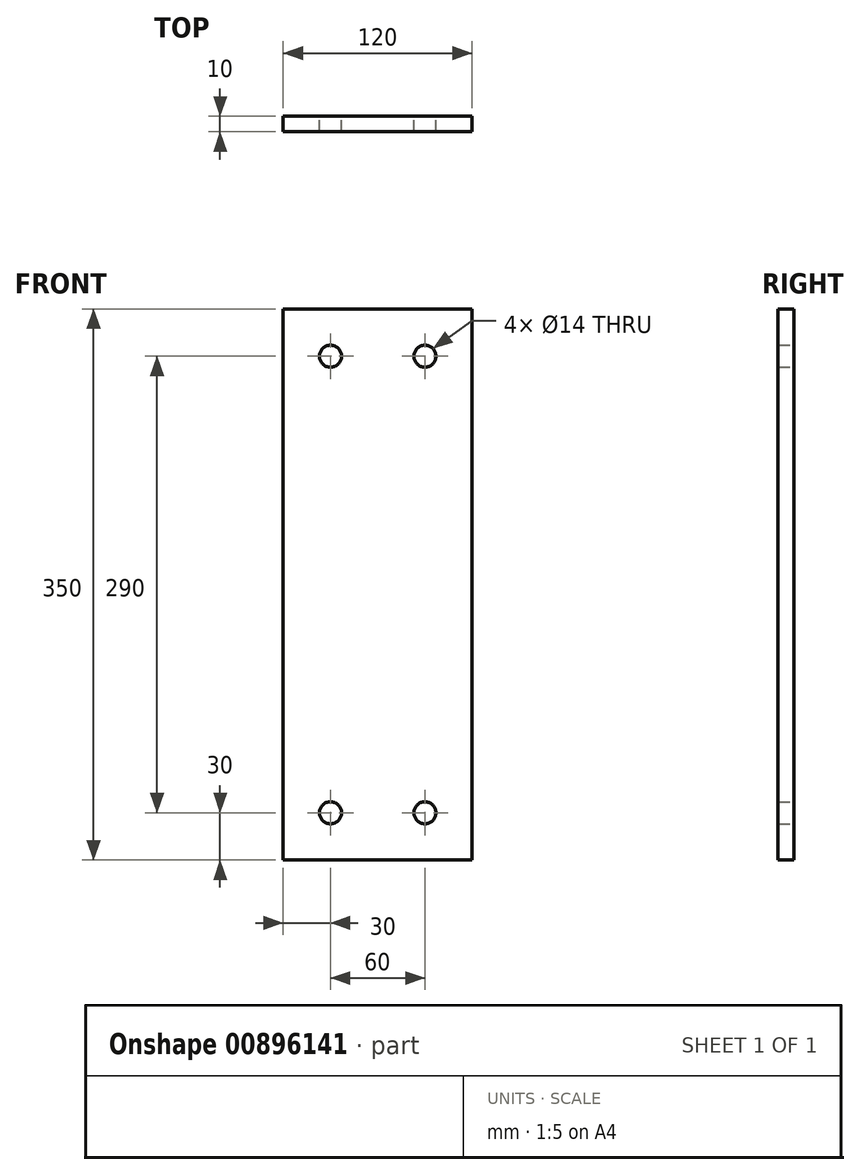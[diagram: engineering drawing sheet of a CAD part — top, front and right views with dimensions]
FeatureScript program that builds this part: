
annotation { "Feature Type Name" : "Feature", "Feature Type Description" : "" }
export const myFeature = defineFeature(function(context is Context, id is Id, definition is map)
    precondition{}
    {
        {
            var Q0;
            Q0=qCreatedBy(makeId("Front.planeOp"),FACE);
            var sketch = newSketch(context, id + "F0", { "sketchPlane" : qUnion([Q0])});
            skLineSegment(sketch, "E0.bottom", {"start": v(60, 175) * mm, "end": v(-60, 175) * mm});
            skLineSegment(sketch, "E0.top", {"start": v(60, -175) * mm, "end": v(-60, -175) * mm});
            skLineSegment(sketch, "E0.left", {"start": v(60, 175) * mm, "end": v(60, -175) * mm});
            skLineSegment(sketch, "E0.right", {"start": v(-60, 175) * mm, "end": v(-60, -175) * mm});
            skPoint(sketch, "E0.middle", {"position": v(0, 0) * mm});
            skCircle(sketch, "E1", {"center": v(-30, 145) * mm, "radius": 7 * mm});
            skCircle(sketch, "E2", {"center": v(30, 145) * mm, "radius": 7 * mm});
            skCircle(sketch, "E3", {"center": v(-30, -145) * mm, "radius": 7 * mm});
            skCircle(sketch, "E4", {"center": v(30, -145) * mm, "radius": 7 * mm});
            skSolve(sketch);
        }
        {
            var Q0;
            Q0=makeQuery(id+"F0.imprint","IMPRINT",FACE,{"disambiguationData":[TD([[makeQuery(id+"F0.imprint","IMPRINT",EDGE,{"derivedFrom":sQuery(id+"F0.wireOp",EDGE,"E0.bottom")}),1.0]])]});
            var Q1;
            Q1=makeQuery(id+"F0.imprint","IMPRINT",FACE,{"disambiguationData":[TD([[makeQuery(id+"F0.imprint","IMPRINT",EDGE,{"derivedFrom":sQuery(id+"F0.wireOp",EDGE,"IxA8HR9I-vB6L-gbE1-t8Bs-stX18FFaMMz4.bottom")}),1.0]])]});
            extrude(context, id + "F1", {"entities" : qUnion([Q0, Q1]), "depth" : 10 * mm, "offsetDistance" : 25 * mm});
        }
    });
